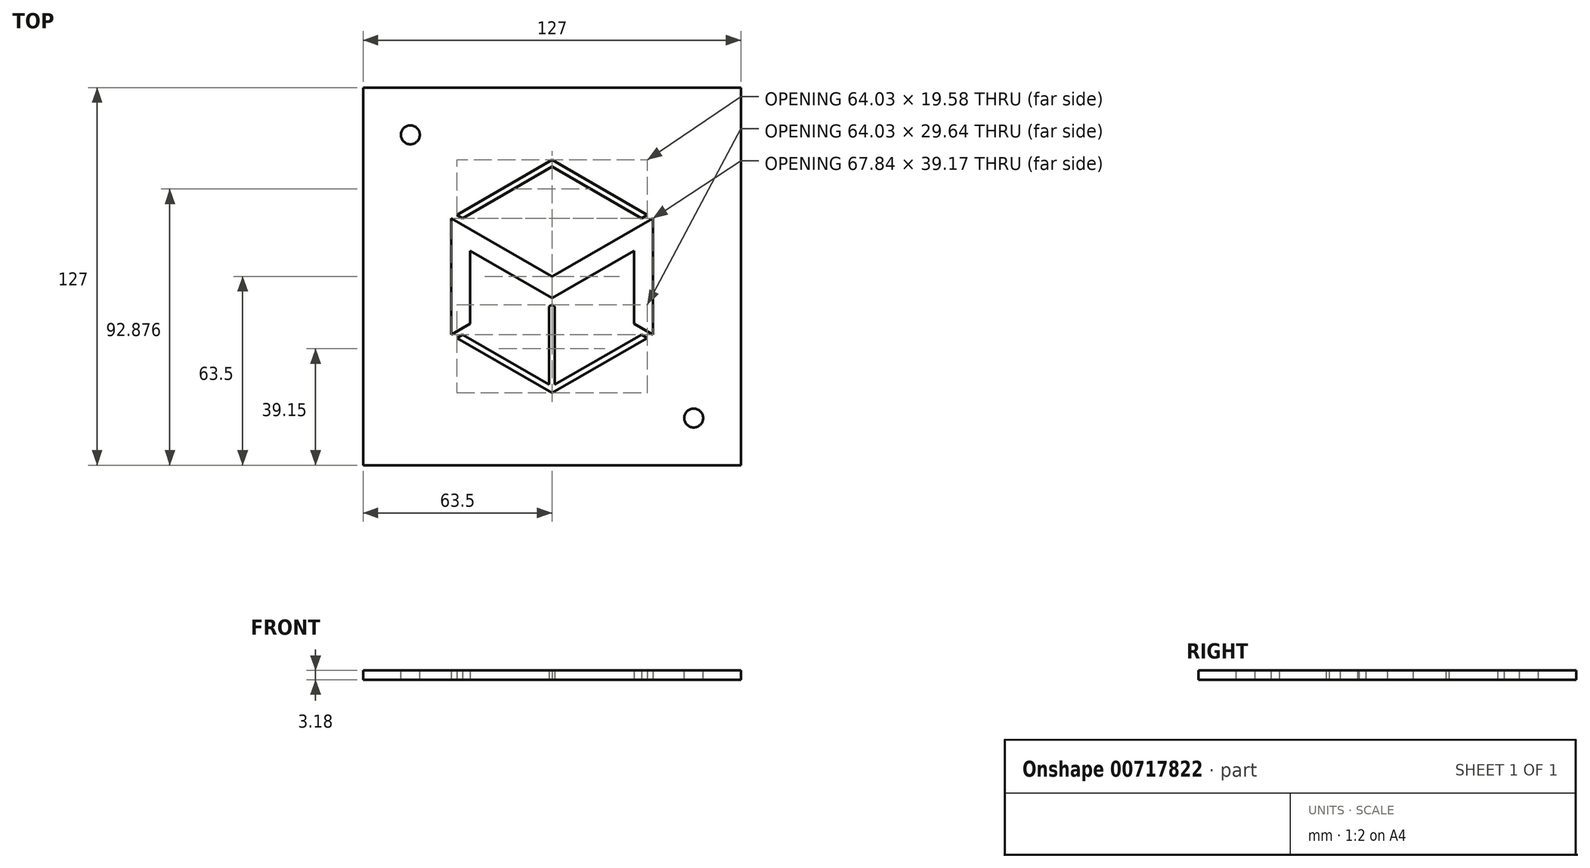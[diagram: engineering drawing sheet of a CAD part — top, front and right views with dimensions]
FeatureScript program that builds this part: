
annotation { "Feature Type Name" : "Feature", "Feature Type Description" : "" }
export const myFeature = defineFeature(function(context is Context, id is Id, definition is map)
    precondition{}
    {
        {
            var Q0;
            Q0=qCreatedBy(makeId("Top.planeOp"),FACE);
            var sketch = newSketch(context, id + "F0", { "sketchPlane" : qUnion([Q0])});
            skCircle(sketch, "E0.cCircle", {"center": v(0, 0) * mm, "radius": 33.92 * mm, "construction": true});
            skLineSegment(sketch, "E0.0", {"start": v(33.92, 19.58) * mm, "end": v(33.92, -19.58) * mm});
            skLineSegment(sketch, "E0.1", {"start": v(33.92, -19.58) * mm, "end": v(0, -39.17) * mm});
            skLineSegment(sketch, "E0.2", {"start": v(0, -39.17) * mm, "end": v(-33.92, -19.58) * mm});
            skLineSegment(sketch, "E0.3", {"start": v(-33.92, -19.58) * mm, "end": v(-33.92, 19.58) * mm});
            skLineSegment(sketch, "E0.4", {"start": v(-33.92, 19.58) * mm, "end": v(0, 39.17) * mm});
            skLineSegment(sketch, "E0.5", {"start": v(0, 39.17) * mm, "end": v(33.92, 19.58) * mm});
            skPoint(sketch, "E0.0.midPoint", {"position": v(33.92, 0) * mm});
            skLineSegment(sketch, "E1", {"start": v(-33.92, 19.58) * mm, "end": v(0, 0) * mm});
            skLineSegment(sketch, "E2", {"start": v(0, 0) * mm, "end": v(33.92, 19.58) * mm});
            skLineSegment(sketch, "E3", {"start": v(27.57, -15.92) * mm, "end": v(33.92, -19.58) * mm});
            skLineSegment(sketch, "E4", {"start": v(-27.57, -15.92) * mm, "end": v(-33.92, -19.58) * mm});
            skLineSegment(sketch, "E5.0", {"start": v(27.57, 8.59) * mm, "end": v(27.57, -15.92) * mm});
            skLineSegment(sketch, "E5.1", {"start": v(0, -7.33) * mm, "end": v(27.57, 8.59) * mm});
            skLineSegment(sketch, "E5.2", {"start": v(-27.57, 8.59) * mm, "end": v(0, -7.33) * mm});
            skLineSegment(sketch, "E5.3", {"start": v(-27.57, -15.92) * mm, "end": v(-27.57, 8.59) * mm});
            skLineSegment(sketch, "E6.0", {"start": v(0, -36.97) * mm, "end": v(-32.97, -17.93) * mm});
            skLineSegment(sketch, "E6.1", {"start": v(32.97, -17.93) * mm, "end": v(0, -36.97) * mm});
            skLineSegment(sketch, "E7.0", {"start": v(-26.62, -17.57) * mm, "end": v(-32.97, -21.23) * mm});
            skLineSegment(sketch, "E8.0", {"start": v(26.62, -17.57) * mm, "end": v(32.97, -21.23) * mm});
            skLineSegment(sketch, "E9.0", {"start": v(0, 36.97) * mm, "end": v(32.97, 17.93) * mm});
            skLineSegment(sketch, "E9.1", {"start": v(-32.97, 17.93) * mm, "end": v(0, 36.97) * mm});
            skLineSegment(sketch, "E10.0", {"start": v(0, 2.2) * mm, "end": v(32.97, 21.23) * mm});
            skLineSegment(sketch, "E10.1", {"start": v(-32.97, 21.23) * mm, "end": v(0, 2.2) * mm});
            skLineSegment(sketch, "E11", {"start": v(0, -7.33) * mm, "end": v(0, -36.97) * mm});
            skLineSegment(sketch, "E12.0", {"start": v(-0.95, -10.08) * mm, "end": v(-0.95, -36.97) * mm});
            skLineSegment(sketch, "E13.0", {"start": v(0.95, -10.08) * mm, "end": v(0.95, -36.97) * mm});
            skLineSegment(sketch, "E14.0", {"start": v(-28.52, 6.94) * mm, "end": v(0.95, -10.08) * mm});
            skLineSegment(sketch, "E15.0", {"start": v(-0.95, -10.08) * mm, "end": v(28.52, 6.94) * mm});
            skSolve(sketch);
        }
        {
            var Q0;
            Q0=qCreatedBy(makeId("Top.planeOp"),FACE);
            var sketch = newSketch(context, id + "F1", { "sketchPlane" : qUnion([Q0])});
            skLineSegment(sketch, "E16.bottom", {"start": v(63.5, 63.5) * mm, "end": v(-63.5, 63.5) * mm});
            skLineSegment(sketch, "E16.top", {"start": v(63.5, -63.5) * mm, "end": v(-63.5, -63.5) * mm});
            skLineSegment(sketch, "E16.left", {"start": v(63.5, 63.5) * mm, "end": v(63.5, -63.5) * mm});
            skLineSegment(sketch, "E16.right", {"start": v(-63.5, 63.5) * mm, "end": v(-63.5, -63.5) * mm});
            skPoint(sketch, "E16.middle", {"position": v(0, 0) * mm});
            skSolve(sketch);
        }
        {
            var Q0;
            Q0 = qSketchRegion(id + "F1", true);
            extrude(context, id + "F2", {"entities" : qUnion([Q0]), "depth" : 3.17 * mm, "offsetDistance" : 25.4 * mm});
        }
        {
            var Q0;
            {var subQ5=sQuery(id+"F0.wireOp",EDGE,"E0.2");var subQ6=sQuery(id+"F0.wireOp",EDGE,"E0.1");var subQ7=makeQuery(id+"F0.imprint","INTERSECT",VERTEX,{"derivedFrom":[subQ6,subQ5]});Q0=makeQuery(id+"F0.imprint","IMPRINT",FACE,{"disambiguationData":[TD([[makeQuery(id+"F0.imprint","IMPRINT",EDGE,{"disambiguationData":[TD([[subQ7,1.0]])],"derivedFrom":subQ6}),-1.0]])]});}
            var Q1;
            {var subQ7=sQuery(id+"F0.wireOp",EDGE,"E0.5");var subQ8=sQuery(id+"F0.wireOp",EDGE,"E0.4");var subQ9=makeQuery(id+"F0.imprint","INTERSECT",VERTEX,{"derivedFrom":[subQ8,subQ7]});Q1=makeQuery(id+"F0.imprint","IMPRINT",FACE,{"disambiguationData":[TD([[makeQuery(id+"F0.imprint","IMPRINT",EDGE,{"disambiguationData":[TD([[subQ9,1.0]])],"derivedFrom":subQ8}),-1.0]])]});}
            var Q2;
            {var subQ4=sQuery(id+"F0.wireOp",EDGE,"E0.0");Q2=makeQuery(id+"F0.imprint","IMPRINT",FACE,{"disambiguationData":[TD([[makeQuery(id+"F0.imprint","IMPRINT",EDGE,{"derivedFrom":subQ4}),-1.0]])]});}
            var Q3;
            {var subQ3=sQuery(id+"F0.wireOp",EDGE,"E13.0");var subQ5=sQuery(id+"F0.wireOp",EDGE,"E14.0");var subQ7=makeQuery(id+"F0.imprint","INTERSECT",VERTEX,{"derivedFrom":[subQ3,subQ5]});Q3=makeQuery(id+"F0.imprint","IMPRINT",FACE,{"disambiguationData":[TD([[makeQuery(id+"F0.imprint","IMPRINT",EDGE,{"disambiguationData":[TD([[subQ7,-1.0]])],"derivedFrom":subQ3}),-1.0]])]});}
            var Q4;
            {var subQ3=sQuery(id+"F0.wireOp",EDGE,"E12.0");var subQ5=sQuery(id+"F0.wireOp",EDGE,"E15.0");var subQ7=makeQuery(id+"F0.imprint","INTERSECT",VERTEX,{"derivedFrom":[subQ3,subQ5]});Q4=makeQuery(id+"F0.imprint","IMPRINT",FACE,{"disambiguationData":[TD([[makeQuery(id+"F0.imprint","IMPRINT",EDGE,{"disambiguationData":[TD([[subQ7,-1.0]])],"derivedFrom":subQ3}),1.0]])]});}
            extrude(context, id + "F3", {"entities" : qUnion([Q0, Q1, Q2, Q3, Q4]), "operationType" : NewBodyOperationType.REMOVE, "depth" : 25.4 * mm, "offsetDistance" : 25.4 * mm});
        }
        {
            var Q0;
            Q0=makeQuery(id+"F2.opExtrude","CAP_FACE",FACE,{"disambiguationData":[OSD([sQuery(id+"F1.wireOp",EDGE,"E16.bottom"),sQuery(id+"F1.wireOp",EDGE,"E16.top"),sQuery(id+"F1.wireOp",EDGE,"E16.left"),sQuery(id+"F1.wireOp",EDGE,"E16.right")])],"isStart":false});
            var sketch = newSketch(context, id + "F4", { "sketchPlane" : qUnion([Q0])});
            skLineSegment(sketch, "E17.bottom", {"start": v(47.63, 47.62) * mm, "end": v(-47.62, 47.62) * mm});
            skLineSegment(sketch, "E17.top", {"start": v(47.63, -47.63) * mm, "end": v(-47.62, -47.63) * mm});
            skLineSegment(sketch, "E17.left", {"start": v(47.63, 47.62) * mm, "end": v(47.63, -47.63) * mm});
            skLineSegment(sketch, "E17.right", {"start": v(-47.62, 47.62) * mm, "end": v(-47.62, -47.63) * mm});
            skPoint(sketch, "E17.middle", {"position": v(0, 0) * mm});
            skCircle(sketch, "E18", {"center": v(-47.62, 47.62) * mm, "radius": 3.18 * mm});
            skCircle(sketch, "E19", {"center": v(47.63, -47.63) * mm, "radius": 3.18 * mm});
            skSolve(sketch);
        }
        {
            var Q0;
            {var subQ0=sQuery(id+"F4.wireOp",EDGE,"E17.right");var subQ1=sQuery(id+"F4.wireOp",EDGE,"E17.bottom");var subQ2=makeQuery(id+"F4.imprint","INTERSECT",VERTEX,{"derivedFrom":[subQ1,subQ0]});Q0=makeQuery(id+"F4.imprint","IMPRINT",FACE,{"disambiguationData":[TD([[makeQuery(id+"F4.imprint","IMPRINT",EDGE,{"disambiguationData":[TD([[subQ2,1.0]])],"derivedFrom":subQ1}),1.0]])]});}
            var Q1;
            {var subQ0=sQuery(id+"F4.wireOp",EDGE,"E17.right");var subQ1=sQuery(id+"F4.wireOp",EDGE,"E17.bottom");var subQ2=makeQuery(id+"F4.imprint","INTERSECT",VERTEX,{"derivedFrom":[subQ1,subQ0]});Q1=makeQuery(id+"F4.imprint","IMPRINT",FACE,{"disambiguationData":[TD([[makeQuery(id+"F4.imprint","IMPRINT",EDGE,{"disambiguationData":[TD([[subQ2,1.0]])],"derivedFrom":subQ1}),-1.0]])]});}
            var Q2;
            {var subQ0=sQuery(id+"F4.wireOp",EDGE,"E17.left");var subQ1=sQuery(id+"F4.wireOp",EDGE,"E17.top");var subQ2=makeQuery(id+"F4.imprint","INTERSECT",VERTEX,{"derivedFrom":[subQ1,subQ0]});Q2=makeQuery(id+"F4.imprint","IMPRINT",FACE,{"disambiguationData":[TD([[makeQuery(id+"F4.imprint","IMPRINT",EDGE,{"disambiguationData":[TD([[subQ2,-1.0]])],"derivedFrom":subQ1}),1.0]])]});}
            var Q3;
            {var subQ0=sQuery(id+"F4.wireOp",EDGE,"E17.left");var subQ1=sQuery(id+"F4.wireOp",EDGE,"E17.top");var subQ2=makeQuery(id+"F4.imprint","INTERSECT",VERTEX,{"derivedFrom":[subQ1,subQ0]});Q3=makeQuery(id+"F4.imprint","IMPRINT",FACE,{"disambiguationData":[TD([[makeQuery(id+"F4.imprint","IMPRINT",EDGE,{"disambiguationData":[TD([[subQ2,-1.0]])],"derivedFrom":subQ1}),-1.0]])]});}
            extrude(context, id + "F5", {"entities" : qUnion([Q0, Q1, Q2, Q3]), "operationType" : NewBodyOperationType.REMOVE, "oppositeDirection" : true, "depth" : 25.4 * mm, "offsetDistance" : 25.4 * mm});
        }
    });
